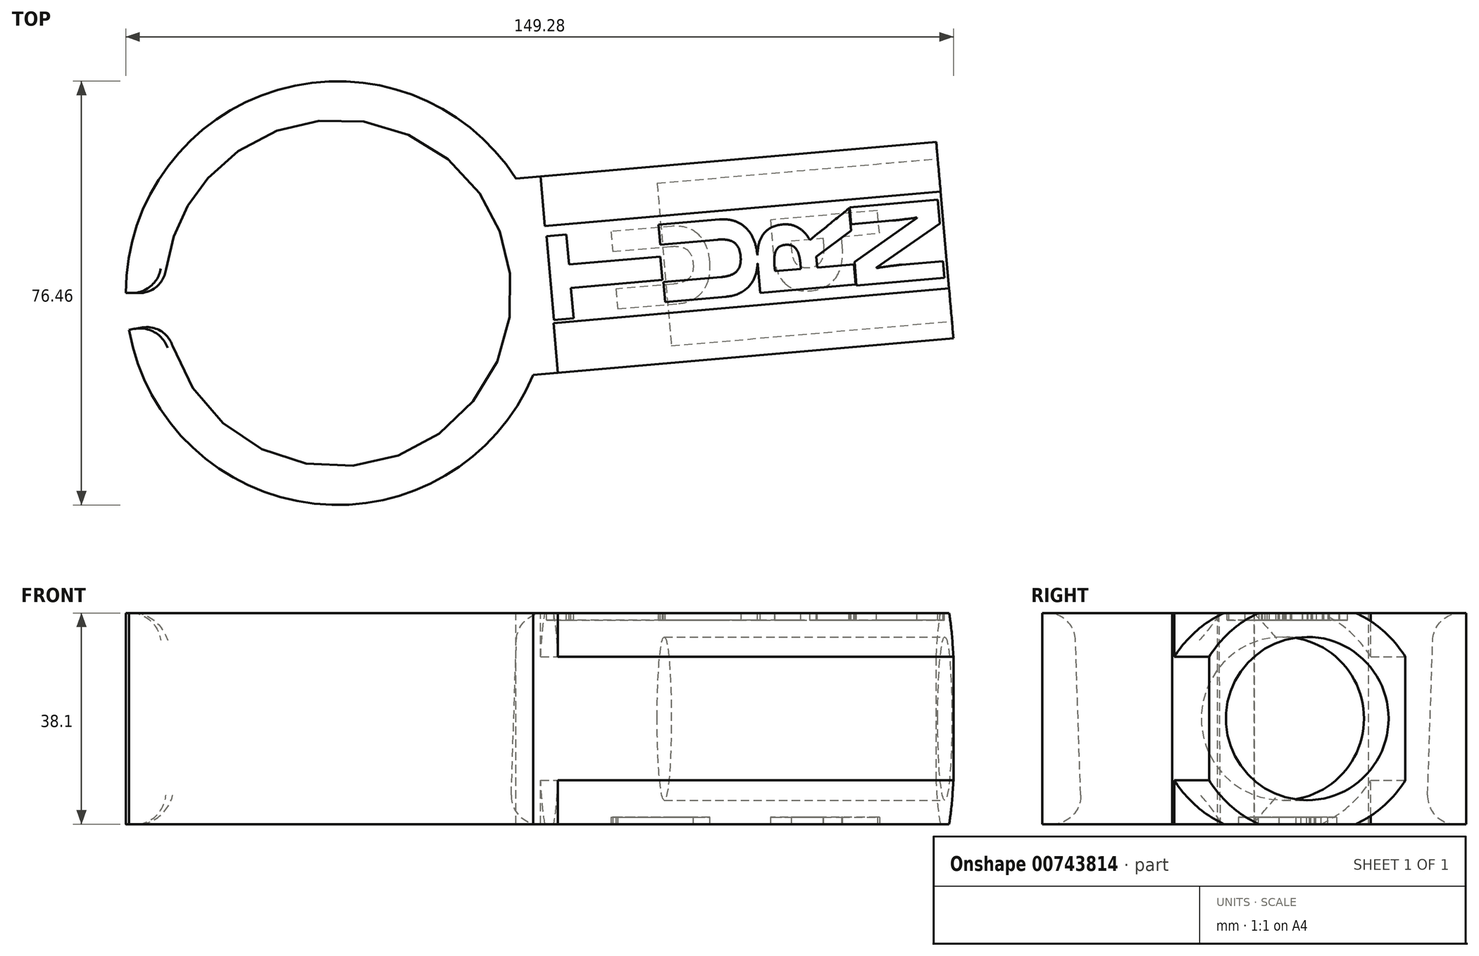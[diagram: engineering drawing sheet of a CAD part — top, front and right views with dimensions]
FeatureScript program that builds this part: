
annotation { "Feature Type Name" : "Feature", "Feature Type Description" : "" }
export const myFeature = defineFeature(function(context is Context, id is Id, definition is map)
    precondition{}
    {
        {
            var Q0;
            Q0=qCreatedBy(makeId("Front.planeOp"),FACE);
            var sketch = newSketch(context, id + "F0", { "sketchPlane" : qUnion([Q0])});
            skLineSegment(sketch, "E0", {"start": v(0, 77.34) * mm, "end": v(0, -73.52) * mm, "construction": true});
            skLineSegment(sketch, "E1", {"start": v(-32.39, 30.5) * mm, "end": v(-38.23, 30.5) * mm});
            skLineSegment(sketch, "E2", {"start": v(-38.23, 30.5) * mm, "end": v(-38.23, -7.6) * mm});
            skLineSegment(sketch, "E3", {"start": v(-38.23, -7.6) * mm, "end": v(-31.11, -7.6) * mm});
            skLineSegment(sketch, "E4", {"start": v(-31.11, -7.6) * mm, "end": v(-32.38, 30.5) * mm});
            skLineSegment(sketch, "E5", {"start": v(-32.39, 30.5) * mm, "end": v(0, 30.5) * mm, "construction": true});
            skLineSegment(sketch, "E6", {"start": v(-31.11, -7.6) * mm, "end": v(0, -7.6) * mm, "construction": true});
            skSolve(sketch);
        }
        {
            var Q0;
            Q0=qSketchRegion(id+"F0",true);
            var Q1;
            Q1=sQuery(id+"F0.wireOp",EDGE,"E0");
            revolve(context, id + "F1", {"entities" : qUnion([Q0]), "axis" : qUnion([Q1]), "revolveType" : RevolveType.ONE_DIRECTION, "angle" : 350 * degree});
        }
        {
            var Q0;
            Q0=makeQuery(id+"F1.opRevolve","SWEPT_FACE",FACE,{"disambiguationData":[OSD([sQuery(id+"F0.wireOp",EDGE,"E1")])]});
            var sketch = newSketch(context, id + "F2", { "sketchPlane" : qUnion([Q0])});
            skLineSegment(sketch, "E7", {"start": v(-37.65, -6.64) * mm, "end": v(31.9, 5.62) * mm, "construction": true});
            skLineSegment(sketch, "E8", {"start": v(-38.23, 0) * mm, "end": v(32.38, 0) * mm, "construction": true});
            skLineSegment(sketch, "E9", {"start": v(35.3, 0) * mm, "end": v(38.23, 0) * mm});
            skLineSegment(sketch, "E10", {"start": v(34.77, 6.13) * mm, "end": v(37.65, 6.64) * mm});
            skLineSegment(sketch, "E11", {"start": v(32.38, 0) * mm, "end": v(35.3, 0) * mm, "construction": true});
            skLineSegment(sketch, "E12", {"start": v(31.9, 5.62) * mm, "end": v(34.77, 6.13) * mm, "construction": true});
            skArc(sketch, "E13", {"start": v(38.23, 0) * mm, "mid": v(38.66, 3.38) * mm, "end": v(37.65, 6.64) * mm});
            skLineSegment(sketch, "E14", {"start": v(33.85, 0) * mm, "end": v(33.33, 5.88) * mm});
            skLineSegment(sketch, "E15", {"start": v(33.85, 0) * mm, "end": v(35.3, 0) * mm});
            skLineSegment(sketch, "E16", {"start": v(33.33, 5.88) * mm, "end": v(34.77, 6.13) * mm});
            skSolve(sketch);
        }
        {
            var Q0;
            Q0=qSketchRegion(id+"F2",true);
            extrude(context, id + "F3", {"entities" : qUnion([Q0]), "operationType" : NewBodyOperationType.REMOVE, "oppositeDirection" : true, "depth" : 49.28 * mm, "offsetDistance" : 25.4 * mm});
        }
        {
            var Q0;
            Q0=makeQuery(id+"F3.boolean.opBoolean","COPY",FACE,{"derivedFrom":makeQuery(id+"F3.opExtrude","SWEPT_FACE",FACE,{"disambiguationData":[OSD([sQuery(id+"F2.wireOp",EDGE,"E14")])]})});
            var sketch = newSketch(context, id + "F4", { "sketchPlane" : qUnion([Q0])});
            skLineSegment(sketch, "E17", {"start": v(-3.33, 30.5) * mm, "end": v(3.33, -7.6) * mm, "construction": true});
            skLineSegment(sketch, "E18", {"start": v(3.33, 30.5) * mm, "end": v(-3.33, -7.6) * mm, "construction": true});
            skPoint(sketch, "E19", {"position": v(0, 11.44) * mm});
            skLineSegment(sketch, "E20.bottom", {"start": v(17.78, -7.6) * mm, "end": v(-17.78, -7.6) * mm});
            skLineSegment(sketch, "E20.top", {"start": v(17.78, 30.5) * mm, "end": v(-17.78, 30.5) * mm});
            skLineSegment(sketch, "E20.left", {"start": v(17.78, -7.6) * mm, "end": v(17.78, 30.5) * mm});
            skLineSegment(sketch, "E20.right", {"start": v(-17.78, -7.6) * mm, "end": v(-17.78, 30.5) * mm});
            skSolve(sketch);
        }
        {
            var Q0;
            Q0=qSketchRegion(id+"F4",true);
            extrude(context, id + "F5", {"entities" : qUnion([Q0]), "operationType" : NewBodyOperationType.ADD, "depth" : 76.2 * mm, "offsetDistance" : 25.4 * mm});
        }
        {
            var Q0;
            Q0=makeQuery(id+"F5.opExtrude","CAP_FACE",FACE,{"disambiguationData":[OSD([sQuery(id+"F4.wireOp",EDGE,"E20.bottom"),sQuery(id+"F4.wireOp",EDGE,"E20.top"),sQuery(id+"F4.wireOp",EDGE,"E20.left"),sQuery(id+"F4.wireOp",EDGE,"E20.right")])],"isStart":false});
            var sketch = newSketch(context, id + "F6", { "sketchPlane" : qUnion([Q0])});
            skLineSegment(sketch, "E21", {"start": v(-17.78, 30.5) * mm, "end": v(17.78, -7.6) * mm, "construction": true});
            skLineSegment(sketch, "E22", {"start": v(17.78, 30.5) * mm, "end": v(-17.78, -7.6) * mm, "construction": true});
            skCircle(sketch, "E23", {"center": v(0, 11.44) * mm, "radius": 14.73 * mm});
            skSolve(sketch);
        }
        {
            var Q0;
            Q0=qSketchRegion(id+"F6",true);
            extrude(context, id + "F7", {"entities" : qUnion([Q0]), "operationType" : NewBodyOperationType.REMOVE, "oppositeDirection" : true, "depth" : 50.8 * mm, "offsetDistance" : 25.4 * mm});
        }
        {
            var Q0;
            Q0=makeQuery(id+"F5.opExtrude","CAP_FACE",FACE,{"disambiguationData":[OSD([sQuery(id+"F4.wireOp",EDGE,"E20.bottom"),sQuery(id+"F4.wireOp",EDGE,"E20.top"),sQuery(id+"F4.wireOp",EDGE,"E20.left"),sQuery(id+"F4.wireOp",EDGE,"E20.right")])],"isStart":false});
            var sketch = newSketch(context, id + "F8", { "sketchPlane" : qUnion([Q0])});
            skCircle(sketch, "E24", {"center": v(0, 11.44) * mm, "radius": 26.06 * mm});
            skCircle(sketch, "E25", {"center": v(0, 11.44) * mm, "radius": 20.98 * mm});
            skSolve(sketch);
        }
        {
            var Q0;
            Q0=qSketchRegion(id+"F8",true);
            extrude(context, id + "F9", {"entities" : qUnion([Q0]), "operationType" : NewBodyOperationType.REMOVE, "oppositeDirection" : true, "depth" : 71.63 * mm, "offsetDistance" : 25.4 * mm});
        }
        {
            var Q0;
            Q0=makeQuery(id+"F5.opExtrude","CAP_EDGE",EDGE,{"disambiguationData":[OSD([sQuery(id+"F4.wireOp",EDGE,"E20.left")])],"isStart":true});
            var Q1;
            Q1=makeQuery(id+"F5.opExtrude","CAP_EDGE",EDGE,{"disambiguationData":[OSD([sQuery(id+"F4.wireOp",EDGE,"E20.right")])],"isStart":true});
            var Q2;
            Q2=makeQuery(id+"F1.opRevolve","CAP_EDGE",EDGE,{"disambiguationData":[OSD([sQuery(id+"F0.wireOp",EDGE,"E4")])],"isStart":true});
            var Q3;
            Q3=makeQuery(id+"F1.opRevolve","CAP_EDGE",EDGE,{"disambiguationData":[OSD([sQuery(id+"F0.wireOp",EDGE,"E4")])],"isStart":false});
            var Q4;
            Q4=makeQuery(id+"F1.opRevolve","SWEPT_EDGE",EDGE,{"disambiguationData":[OSD([sQuery(id+"F0.wireOp",EDGE,"E1"),sQuery(id+"F0.wireOp",EDGE,"E4")])]});
            var Q5;
            Q5=makeQuery(id+"F1.opRevolve","SWEPT_EDGE",EDGE,{"disambiguationData":[OSD([sQuery(id+"F0.wireOp",EDGE,"E3"),sQuery(id+"F0.wireOp",EDGE,"E4")])]});
            fillet(context, id + "F10", {"entities" : qUnion([Q0, Q1, Q2, Q3, Q4, Q5]), "radius" : 5.08 * mm, "tangentPropagation" : true, "allowEdgeOverflow" : false});
        }
        {
            var Q0;
            Q0=makeQuery(id+"F5.boolean.opBoolean","MERGE",FACE,{"derivedFrom":[makeQuery(id+"F1.opRevolve","SWEPT_FACE",FACE,{"disambiguationData":[OSD([sQuery(id+"F0.wireOp",EDGE,"E3")])]}),makeQuery(id+"F5.opExtrude","SWEPT_FACE",FACE,{"disambiguationData":[OSD([sQuery(id+"F4.wireOp",EDGE,"E20.bottom")])]})]});
            var sketch = newSketch(context, id + "F11", { "sketchPlane" : qUnion([Q0])});
            skText(sketch, "E26", { "text": "U", "fontName": "OpenSans-Bold.ttf"});
            skText(sketch, "E27", { "text": "P", "fontName": "OpenSans-Bold.ttf"});
            skLineSegment(sketch, "E28", {"start": v(38.9, 5.41) * mm, "end": v(50.5, 4.4) * mm, "construction": true});
            skLineSegment(sketch, "E29", {"start": v(67.63, 2.9) * mm, "end": v(79.22, 1.89) * mm, "construction": true});
            skLineSegment(sketch, "E30", {"start": v(98.67, 0.19) * mm, "end": v(110.26, -0.83) * mm, "construction": true});
            const initialGuessF11  = {"E26": [0.0661, -0.0146, 0.08716, 0.9962, 0.0172], "E27": [0.09714, -0.01732, 0.08716, 0.9962, 0.01953]};
            skSetInitialGuess(sketch, initialGuessF11);
            skSolve(sketch);
        }
        {
            var Q0;
            Q0 = qSketchRegion(id + "F11", true);
            extrude(context, id + "F12", {"entities" : qUnion([Q0]), "operationType" : NewBodyOperationType.REMOVE, "oppositeDirection" : true, "depth" : 1.27 * mm, "offsetDistance" : 25.4 * mm});
        }
        {
            var Q0;
            Q0=makeQuery(id+"F5.boolean.opBoolean","MERGE",FACE,{"derivedFrom":[makeQuery(id+"F1.opRevolve","SWEPT_FACE",FACE,{"disambiguationData":[OSD([sQuery(id+"F0.wireOp",EDGE,"E1")])]}),makeQuery(id+"F5.opExtrude","SWEPT_FACE",FACE,{"disambiguationData":[OSD([sQuery(id+"F4.wireOp",EDGE,"E20.top")])]})]});
            var sketch = newSketch(context, id + "F13", { "sketchPlane" : qUnion([Q0])});
            skText(sketch, "E31", { "text": "N", "fontName": "OpenSans-Bold.ttf"});
            skText(sketch, "E32", { "text": "T", "fontName": "OpenSans-Bold.ttf"});
            skText(sketch, "E33", { "text": "U", "fontName": "OpenSans-Bold.ttf"});
            skText(sketch, "E34", { "text": "R", "fontName": "OpenSans-Bold.ttf"});
            const initialGuessF13  = {"E31": [0.10961, 0.00077, -0.08716, 0.9962, 0.01606], "E32": [0.0591, -0.00365, -0.08716, 0.9962, 0.02028], "E33": [0.07624, -0.00215, -0.08716, 0.9962, 0.0172], "E34": [0.09362, -0.00063, -0.08716, 0.9962, 0.01745]};
            skSetInitialGuess(sketch, initialGuessF13);
            skSolve(sketch);
        }
        {
            var Q0;
            Q0 = qSketchRegion(id + "F13", true);
            extrude(context, id + "F14", {"entities" : qUnion([Q0]), "operationType" : NewBodyOperationType.REMOVE, "oppositeDirection" : true, "depth" : 1.27 * mm, "offsetDistance" : 25.4 * mm});
        }
    });
